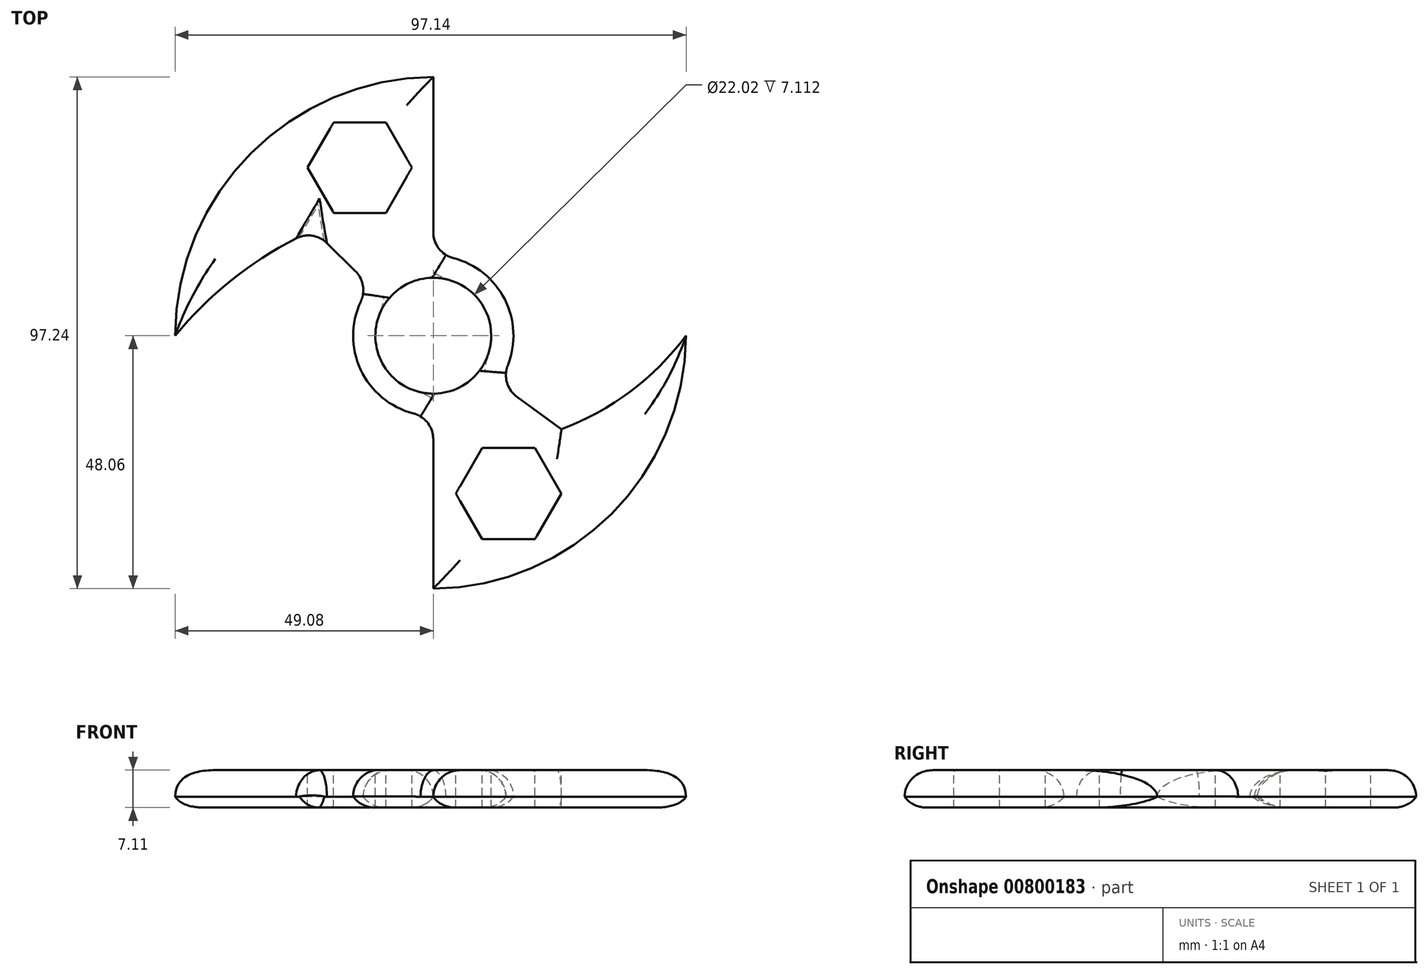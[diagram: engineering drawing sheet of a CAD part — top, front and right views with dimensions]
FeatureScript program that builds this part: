
annotation { "Feature Type Name" : "Feature", "Feature Type Description" : "" }
export const myFeature = defineFeature(function(context is Context, id is Id, definition is map)
    precondition{}
    {
        {
            var Q0;
            Q0=qCreatedBy(makeId("Top.planeOp"),FACE);
            var sketch = newSketch(context, id + "F0", { "sketchPlane" : qUnion([Q0])});
            skCircle(sketch, "E0", {"center": v(0, 0) * mm, "radius": 11.01 * mm});
            skCircle(sketch, "E1", {"center": v(0, 0) * mm, "radius": 3.98 * mm});
            skCircle(sketch, "E2", {"center": v(0, 0) * mm, "radius": 15.24 * mm});
            skSolve(sketch);
        }
        {
            var Q0;
            Q0=makeQuery(id+"F0.imprint","IMPRINT",FACE,{"disambiguationData":[TD([[makeQuery(id+"F0.imprint","IMPRINT",EDGE,{"derivedFrom":sQuery(id+"F0.wireOp",EDGE,"E0")}),-1.0]])]});
            extrude(context, id + "F1", {"entities" : qUnion([Q0]), "oppositeDirection" : true, "depth" : 7.11 * mm, "offsetDistance" : 25.4 * mm});
        }
        {
            var Q0;
            Q0=qCreatedBy(makeId("Top.planeOp"),FACE);
            var sketch = newSketch(context, id + "F2", { "sketchPlane" : qUnion([Q0])});
            skLineSegment(sketch, "E3", {"start": v(-24.02, 31.94) * mm, "end": v(-3.95, 31.94) * mm});
            skCircle(sketch, "E4.cCircle", {"center": v(-13.98, 31.94) * mm, "radius": 8.59 * mm, "construction": true});
            skLineSegment(sketch, "E4.0", {"start": v(-18.94, 40.53) * mm, "end": v(-9.02, 40.53) * mm});
            skLineSegment(sketch, "E4.1", {"start": v(-9.02, 40.53) * mm, "end": v(-4.07, 31.94) * mm});
            skLineSegment(sketch, "E4.2", {"start": v(-4.07, 31.94) * mm, "end": v(-9.02, 23.35) * mm});
            skLineSegment(sketch, "E4.3", {"start": v(-9.02, 23.35) * mm, "end": v(-18.94, 23.35) * mm});
            skLineSegment(sketch, "E4.4", {"start": v(-18.94, 23.35) * mm, "end": v(-23.9, 31.94) * mm});
            skLineSegment(sketch, "E4.5", {"start": v(-23.9, 31.94) * mm, "end": v(-18.94, 40.53) * mm});
            skPoint(sketch, "E4.0.midPoint", {"position": v(-13.98, 40.53) * mm});
            skCircle(sketch, "E5.cCircle", {"center": v(14.3, -30) * mm, "radius": 8.69 * mm, "construction": true});
            skLineSegment(sketch, "E5.0", {"start": v(9.3, -21.3) * mm, "end": v(19.32, -21.3) * mm});
            skLineSegment(sketch, "E5.1", {"start": v(19.32, -21.3) * mm, "end": v(24.34, -30) * mm});
            skLineSegment(sketch, "E5.2", {"start": v(24.34, -30) * mm, "end": v(19.32, -38.68) * mm});
            skLineSegment(sketch, "E5.3", {"start": v(19.32, -38.68) * mm, "end": v(9.3, -38.68) * mm});
            skLineSegment(sketch, "E5.4", {"start": v(9.3, -38.68) * mm, "end": v(4.27, -30) * mm});
            skLineSegment(sketch, "E5.5", {"start": v(4.27, -30) * mm, "end": v(9.3, -21.3) * mm});
            skPoint(sketch, "E5.0.midPoint", {"position": v(14.3, -21.3) * mm});
            skSolve(sketch);
        }
        {
            var Q0;
            Q0=qCreatedBy(makeId("Top.planeOp"),FACE);
            var sketch = newSketch(context, id + "F3", { "sketchPlane" : qUnion([Q0])});
            skLineSegment(sketch, "E6", {"start": v(0, 49.18) * mm, "end": v(0, 13.47) * mm});
            skLineSegment(sketch, "E7", {"start": v(-10.67, 8.21) * mm, "end": v(-22.75, 20.09) * mm});
            skArc(sketch, "E8", {"start": v(-22.75, 20.09) * mm, "mid": v(-37.08, 11.57) * mm, "end": v(-49.08, 0) * mm});
            skArc(sketch, "E9", {"start": v(0, 49.18) * mm, "mid": v(-34.65, 34.68) * mm, "end": v(-49.08, 0) * mm});
            skLineSegment(sketch, "E10", {"start": v(0, -13.35) * mm, "end": v(0, -48.06) * mm});
            skArc(sketch, "E11", {"start": v(0, -48.06) * mm, "mid": v(33.87, -33.87) * mm, "end": v(48.06, 0) * mm});
            skLineSegment(sketch, "E12", {"start": v(10.8, -7.88) * mm, "end": v(24.36, -17.75) * mm});
            skArc(sketch, "E13", {"start": v(24.36, -17.75) * mm, "mid": v(37.49, -10.58) * mm, "end": v(48.06, 0) * mm});
            skArc(sketch, "E14", {"start": v(0, 13.47) * mm, "mid": v(-5.94, 12.06) * mm, "end": v(-10.67, 8.21) * mm});
            skArc(sketch, "E15", {"start": v(0, -13.35) * mm, "mid": v(6.12, -12.03) * mm, "end": v(10.8, -7.88) * mm});
            skSolve(sketch);
        }
        {
            var Q0;
            Q0 = qSketchRegion(id + "F3", true);
            extrude(context, id + "F4", {"entities" : qUnion([Q0]), "operationType" : NewBodyOperationType.ADD, "oppositeDirection" : true, "depth" : 7.11 * mm, "offsetDistance" : 25.4 * mm});
        }
        {
            var Q0;
            Q0 = qSketchRegion(id + "F2", true);
            extrude(context, id + "F5", {"entities" : qUnion([Q0]), "operationType" : NewBodyOperationType.REMOVE, "oppositeDirection" : true, "depth" : 7.11 * mm, "offsetDistance" : 25.4 * mm});
        }
        {
            var Q0;
            Q0=makeQuery(id+"F4.boolean.opBoolean","INTERSECT",EDGE,{"derivedFrom":[makeQuery(id+"F1.opExtrude","SWEPT_FACE",FACE,{"disambiguationData":[OSD([sQuery(id+"F0.wireOp",EDGE,"E2")])]}),makeQuery(id+"F4.opExtrude","SWEPT_FACE",FACE,{"disambiguationData":[OSD([sQuery(id+"F3.wireOp",EDGE,"E6")])]})]});
            var Q1;
            Q1=makeQuery(id+"F4.boolean.opBoolean","INTERSECT",EDGE,{"derivedFrom":[makeQuery(id+"F1.opExtrude","SWEPT_FACE",FACE,{"disambiguationData":[OSD([sQuery(id+"F0.wireOp",EDGE,"E2")])]}),makeQuery(id+"F4.opExtrude","SWEPT_FACE",FACE,{"disambiguationData":[OSD([sQuery(id+"F3.wireOp",EDGE,"E12")])]})]});
            var Q2;
            Q2=makeQuery(id+"F4.boolean.opBoolean","INTERSECT",EDGE,{"derivedFrom":[makeQuery(id+"F1.opExtrude","SWEPT_FACE",FACE,{"disambiguationData":[OSD([sQuery(id+"F0.wireOp",EDGE,"E2")])]}),makeQuery(id+"F4.opExtrude","SWEPT_FACE",FACE,{"disambiguationData":[OSD([sQuery(id+"F3.wireOp",EDGE,"E7")])]})]});
            var Q3;
            Q3=makeQuery(id+"F4.boolean.opBoolean","INTERSECT",EDGE,{"derivedFrom":[makeQuery(id+"F1.opExtrude","SWEPT_FACE",FACE,{"disambiguationData":[OSD([sQuery(id+"F0.wireOp",EDGE,"E2")])]}),makeQuery(id+"F4.opExtrude","SWEPT_FACE",FACE,{"disambiguationData":[OSD([sQuery(id+"F3.wireOp",EDGE,"E10")])]})]});
            fillet(context, id + "F6", {"entities" : qUnion([Q0, Q1, Q2, Q3]), "radius" : 5.08 * mm, "tangentPropagation" : true, "defaultsChanged" : false, "vertexSettings" : [], "allowEdgeOverflow" : false});
        }
        {
            var Q0;
            Q0=makeQuery(id+"F4.opExtrude","CAP_EDGE",EDGE,{"disambiguationData":[OSD([sQuery(id+"F3.wireOp",EDGE,"E9")])],"isStart":true});
            var Q1;
            Q1=makeQuery(id+"F4.opExtrude","CAP_EDGE",EDGE,{"disambiguationData":[OSD([sQuery(id+"F3.wireOp",EDGE,"E8")])],"isStart":true});
            var Q2;
            Q2=makeQuery(id+"F4.opExtrude","CAP_EDGE",EDGE,{"disambiguationData":[OSD([sQuery(id+"F3.wireOp",EDGE,"E6")])],"isStart":true});
            var Q3;
            Q3=makeQuery(id+"F4.opExtrude","CAP_EDGE",EDGE,{"disambiguationData":[OSD([sQuery(id+"F3.wireOp",EDGE,"E11")])],"isStart":true});
            var Q4;
            Q4=makeQuery(id+"F4.opExtrude","CAP_EDGE",EDGE,{"disambiguationData":[OSD([sQuery(id+"F3.wireOp",EDGE,"E10")])],"isStart":true});
            var Q5;
            Q5=makeQuery(id+"F4.opExtrude","CAP_EDGE",EDGE,{"disambiguationData":[OSD([sQuery(id+"F3.wireOp",EDGE,"E13")])],"isStart":true});
            fillet(context, id + "F7", {"entities" : qUnion([Q0, Q1, Q2, Q3, Q4, Q5]), "radius" : 5.08 * mm, "tangentPropagation" : true, "allowEdgeOverflow" : false});
        }
        {
            var Q0;
            Q0=makeQuery(id+"F4.opExtrude","CAP_EDGE",EDGE,{"disambiguationData":[OSD([sQuery(id+"F3.wireOp",EDGE,"E10")])],"isStart":false});
            var Q1;
            Q1=makeQuery(id+"F4.opExtrude","CAP_EDGE",EDGE,{"disambiguationData":[OSD([sQuery(id+"F3.wireOp",EDGE,"E11")])],"isStart":false});
            var Q2;
            Q2=makeQuery(id+"F4.opExtrude","CAP_EDGE",EDGE,{"disambiguationData":[OSD([sQuery(id+"F3.wireOp",EDGE,"E13")])],"isStart":false});
            var Q3;
            Q3=makeQuery(id+"F4.opExtrude","CAP_EDGE",EDGE,{"disambiguationData":[OSD([sQuery(id+"F3.wireOp",EDGE,"E12")])],"isStart":false});
            var Q4;
            Q4=makeQuery(id+"F4.opExtrude","CAP_EDGE",EDGE,{"disambiguationData":[OSD([sQuery(id+"F3.wireOp",EDGE,"E6")])],"isStart":false});
            var Q5;
            Q5=makeQuery(id+"F4.opExtrude","CAP_EDGE",EDGE,{"disambiguationData":[OSD([sQuery(id+"F3.wireOp",EDGE,"E8")])],"isStart":false});
            var Q6;
            Q6=makeQuery(id+"F4.opExtrude","CAP_EDGE",EDGE,{"disambiguationData":[OSD([sQuery(id+"F3.wireOp",EDGE,"E9")])],"isStart":false});
            fillet(context, id + "F8", {"entities" : qUnion([Q0, Q1, Q2, Q3, Q4, Q5, Q6]), "radius" : 5.08 * mm, "tangentPropagation" : true, "allowEdgeOverflow" : false});
        }
        {
            var Q0;
            Q0=makeQuery(id+"F7.opFillet","BLEND_EDGE",EDGE,{"blendedFrom":[makeQuery(id+"F4.opExtrude","CAP_EDGE",EDGE,{"disambiguationData":[OSD([sQuery(id+"F3.wireOp",EDGE,"E8")])],"isStart":true}),makeQuery(id+"F4.opExtrude","CAP_EDGE",EDGE,{"disambiguationData":[OSD([sQuery(id+"F3.wireOp",EDGE,"E7")])],"isStart":true})],"blendedInto":[]});
            var Q1;
            Q1=makeQuery(id+"F8.opFillet","BLEND_EDGE",EDGE,{"blendedFrom":[makeQuery(id+"F4.opExtrude","CAP_EDGE",EDGE,{"disambiguationData":[OSD([sQuery(id+"F3.wireOp",EDGE,"E8")])],"isStart":false}),makeQuery(id+"F4.opExtrude","CAP_EDGE",EDGE,{"disambiguationData":[OSD([sQuery(id+"F3.wireOp",EDGE,"E7")])],"isStart":false})],"blendedInto":[]});
            fillet(context, id + "F9", {"entities" : qUnion([Q0, Q1]), "radius" : 5.08 * mm, "tangentPropagation" : true, "allowEdgeOverflow" : false});
        }
    });
